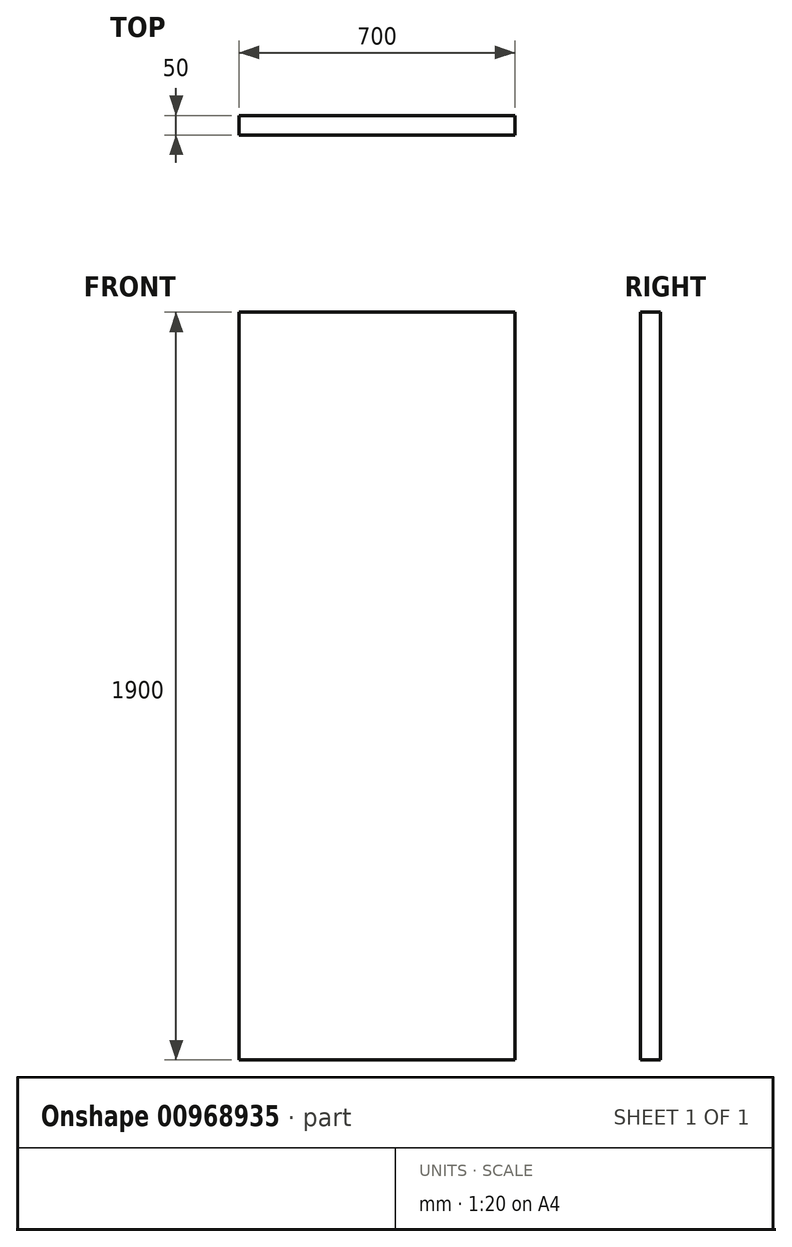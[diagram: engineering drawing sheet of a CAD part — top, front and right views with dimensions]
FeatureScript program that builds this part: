
annotation { "Feature Type Name" : "Feature", "Feature Type Description" : "" }
export const myFeature = defineFeature(function(context is Context, id is Id, definition is map)
    precondition{}
    {
        {
            var Q0;
            Q0=qCreatedBy(makeId("Top.planeOp"),FACE);
            var sketch = newSketch(context, id + "F0", { "sketchPlane" : qUnion([Q0])});
            skLineSegment(sketch, "E0.bottom", {"start": v(350, 25) * mm, "end": v(-350, 25) * mm});
            skLineSegment(sketch, "E0.top", {"start": v(350, -25) * mm, "end": v(-350, -25) * mm});
            skLineSegment(sketch, "E0.left", {"start": v(350, 25) * mm, "end": v(350, -25) * mm});
            skLineSegment(sketch, "E0.right", {"start": v(-350, 25) * mm, "end": v(-350, -25) * mm});
            skPoint(sketch, "E0.middle", {"position": v(0, 0) * mm});
            skSolve(sketch);
        }
        {
            var Q0;
            Q0 = qSketchRegion(id + "F0", true);
            extrude(context, id + "F1", {"entities" : qUnion([Q0]), "depth" : 1900 * mm, "offsetDistance" : 25 * mm});
        }
    });
